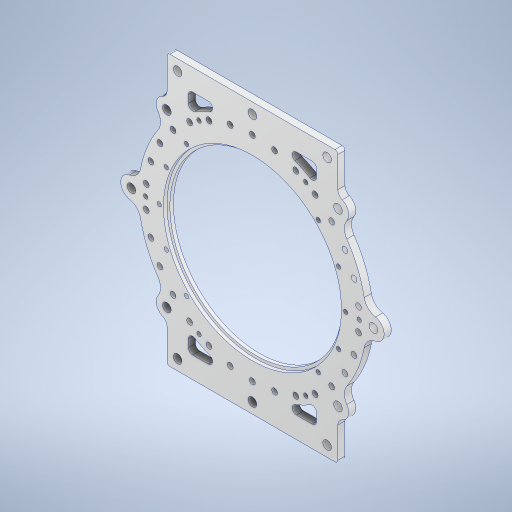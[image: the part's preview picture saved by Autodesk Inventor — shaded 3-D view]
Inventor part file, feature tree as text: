
AUTODESK INVENTOR PART (.ipt)
format: ipt  version: 2024 (Build 280153000, 153)  size: 694,784 bytes
history: native  units: mm
features: thread x11, sketch x11, extrude x6, hole x5, pattern_circular x3, fillet x2, projected_geometry x2, other x1
ambient origin geometry x8: Origin, YZ Plane, XZ Plane, XY Plane, X Axis, Y Axis, Z Axis, Center Point
bodies: Body1 (feature_tree)
feature tree (41):
  other  "ソリッド1"
  extrude  "押し出し1"  Depth=160.0mm
  extrude  "押し出し2"  Depth=5.0mm TaperAngle=0.0deg
  hole  "穴1"  [1 undecoded]
  pattern_circular  "円形状パターン1"  [2 undecoded]
  extrude  "押し出し3"  Depth=75.0mm
  hole  "穴2"  [1 undecoded]
  thread  "ねじ1"
  thread  "ねじ2"
  thread  "ねじ3"
  thread  "ねじ4"
  thread  "ねじ5"
  thread  "ねじ6"
  thread  "ねじ7"
  thread  "ねじ8"
  thread  "ねじ9"
  thread  "ねじ10"
  hole  "穴3"  [1 undecoded]
  thread  "ねじ11"
  pattern_circular  "円形状パターン2"  [2 undecoded]
  extrude  "押し出し4"  Depth=2.5mm TaperAngle=0.0deg
  hole  "穴4"  [1 undecoded]
  pattern_circular  "円形状パターン3"  [2 undecoded]
  extrude  "押し出し5"  Depth=160.0mm TaperAngle=360.0deg
  hole  "穴5"  [1 undecoded]
  fillet  "フィレット1"  Radius=5.0mm
  fillet  "フィレット2"  Radius=5.0mm
  extrude  "押し出し6"  Depth=5.0mm TaperAngle=0.0deg
  sketch  "スケッチ1"
  sketch  "スケッチ2"
  sketch  "スケッチ3"
  sketch  "スケッチ4"
  sketch  "スケッチ5"
  sketch  "スケッチ6"
  sketch  "スケッチ7"
  sketch  "スケッチ8"
  sketch  "スケッチ9"
  projected_geometry  "投影ループ1"
  sketch  "スケッチ10"
  sketch  "スケッチ11"
  projected_geometry  "投影ループ2"
note: 11 required parameter values undecoded (feature->parameter linkage not recoverable at this tier; creation-order binding heuristic only, values carry confidence <= 0.55)
